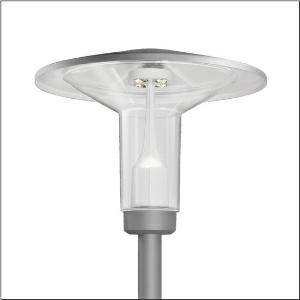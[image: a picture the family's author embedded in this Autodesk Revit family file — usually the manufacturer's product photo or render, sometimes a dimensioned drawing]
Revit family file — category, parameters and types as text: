
# Revit family: laterne_iq___p1_0a_5xa5255ff14h_2151
name_source: partatom
category: Lighting Fixtures
units: mm (PartAtom-declared; Revit-internal decimal feet)

## family parameters
Cut with Voids When Loaded = No
Host = Face
Light Source = No
Part Type = Normal
Room Calculation Point = No
Round Connector Dimension = Use Diameter
Shared = No

## types (1)
- --- (1 x LED, 1510 lm, 10.5 W, 3000K)
    Apparent Load = 11 VA
    CIE Flux Codes = 35 64 91 96 100
    Color Rendering = 70
    Color Temperature = 3000K
    Default Elevation = 1800 mm
    Description = Lantern iQ, mast luminaire, Module 540 iQ-SR, primary light control with 3 zone facetted reflector, of plastic, silver coated, highly specular, structured, primary optical cover: cover, of PMMA, transparent, light distribution: P1.0a, light emission: direct distribution, primary light characteristic: strongly asymmetric, installation type: post-top, LED, High Power LED, rated luminous flux: 1.510lm, luminous efficacy: 144lm/W, light colour: 730, colour temperature: 3000K, control gear: ECG iQ, control: Auto-Match, Temp-Guard, Lumen-Switch, Night-Set, Smart-Wire, Light-Fading, Desk-Remote (wireless, voltage-free reading and setting of iQ features in the workshop via application-optimized NFC function/RFID function), optimised constant luminous flux control (CLO 2.0), Street-Remote, pre-setting: logarithmic dimming characteristic, with terminal, 6-pole, max. 2.5mm², mains connection: 230..240V, AC, 50/60Hz, start of lifetime: 11W, end of service life: 11W, reduction: 5W, luminaire housing, upper part, of glass-fibre reinforced polyester, coated, Siteco® metallic grey (DB 702S), diameter: 750mm, height: 583mm, spigot size: d x l = 76 x 70mm (post-top) | with reducer (optional accessory) 60 x 70mm, post-top mast mounting element, of diecast aluminium, coated, Siteco® metallic grey (DB 702S), Module 540 iQ-SR, traffic white (RAL 9016), equipment: standard, protection rating (complete): IP65, insulation class (complete): insulation class II (safety insulation), certification: CE, ENEC, VDE, packaging unit: 1 piece

Light Distribution: P1.0a
    Height = 583 mm
    Lamp = 1 x LED
    Lamp Light Flux = 1510 lm
    Lamp Power = 10.5 W
    Lamp count = 1
    Length = 750 mm
    Luminous efficacy = 144 lm/W
    Manufacturer = Siteco
    ModVariant = No
    Model = 5XA5255FF14H
    Number of Poles = 1
    OnlyDefault = Yes
    Power Factor = 1
    Product Name = Laterne iQ | P1.0a
    Product group = mast luminaire | pylon top
    ProductGroupID = 6100
    Protection Class = Protection class II
    Protection Degree = IP 65
    RLX_Detail_Level = 1
    RLX_Emergency_Light_Flux = 0 lm
    RLX_Emergency_Type = 0
    RLX_Emergency_Type_DB = No
    RlxData = <blob elided: 74157 chars, md5=8a76c648>
    Socket = socket
    Standby Power = 0 W
    System Light Flux = 1510 lm
    System Power = 11 W
    Type Comments = factory setting: luminous flux: 100 % | dim-lin: 254 | 419 mA
    Type Image = l_1006050.jpg
    URL = http://relux.com
    VarID = @adj_130863
    Voltage = 0 V
    Weight = 0.00 kg
    Width = 0 mm  [stored 0 ft]

note: [stored X ft] marks values corroborated as IEEE doubles in the binary element streams (Revit-internal decimal feet)

## geometry (parser evidence)
native form markers: Blend x4, Sweep x9
no freeform markers — native parametric forms only
